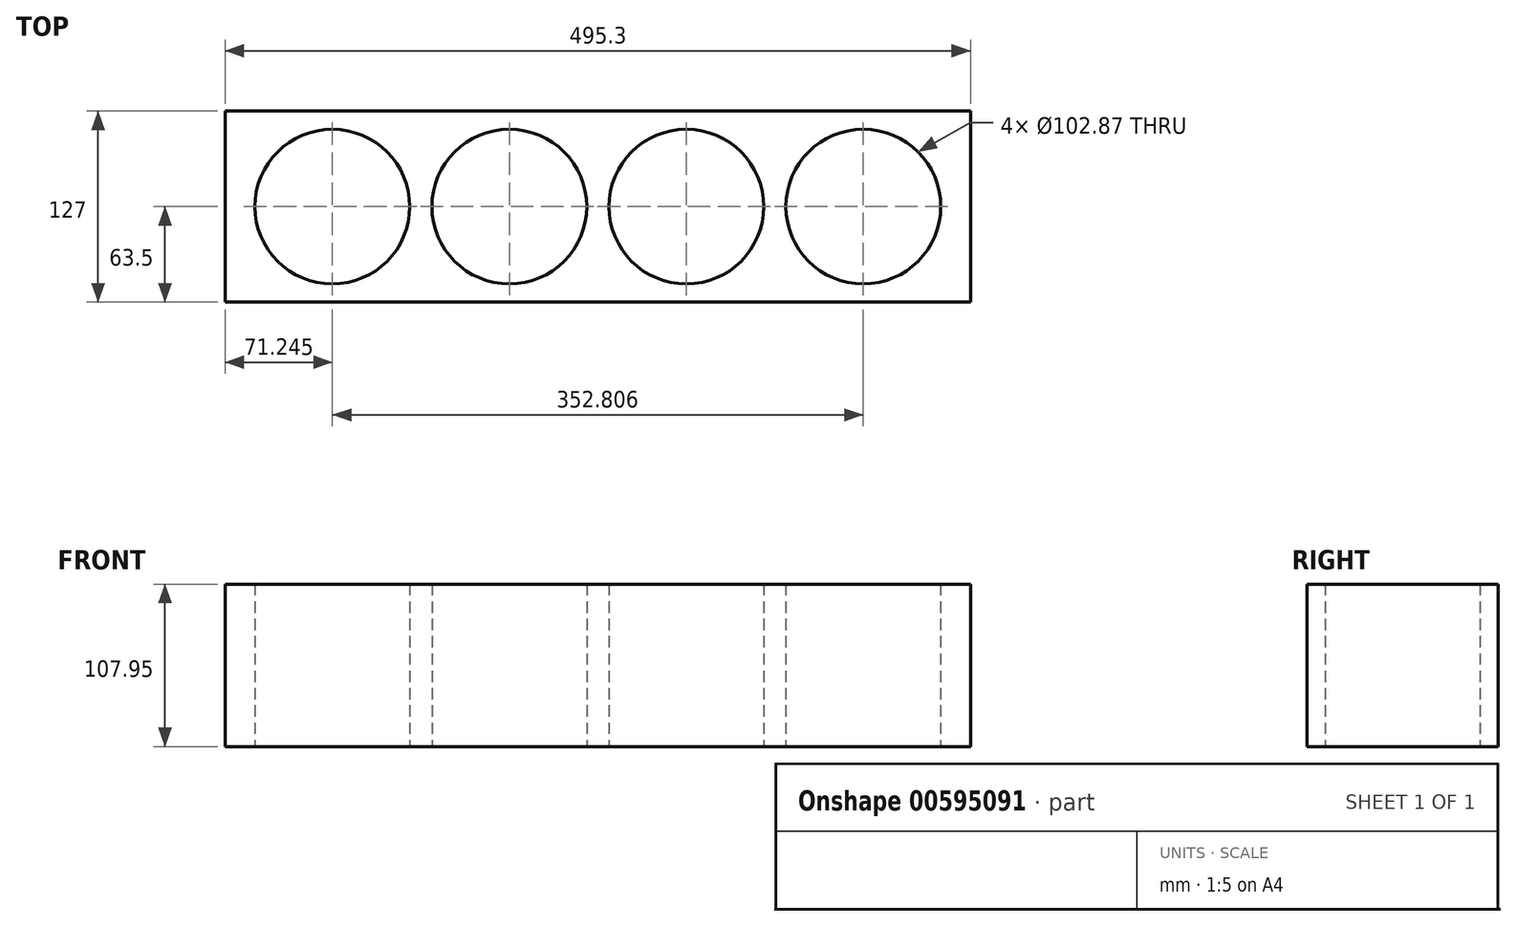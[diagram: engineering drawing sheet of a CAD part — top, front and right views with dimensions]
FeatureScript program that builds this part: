
annotation { "Feature Type Name" : "Feature", "Feature Type Description" : "" }
export const myFeature = defineFeature(function(context is Context, id is Id, definition is map)
    precondition{}
    {
        {
            var Q0;
            Q0=qCreatedBy(makeId("Top.planeOp"),FACE);
            var sketch = newSketch(context, id + "F0", { "sketchPlane" : qUnion([Q0])});
            skCircle(sketch, "E0", {"center": v(-223.26, 0) * mm, "radius": 51.44 * mm});
            skCircle(sketch, "E1.1.0.0", {"center": v(-105.66, 0) * mm, "radius": 51.44 * mm});
            skCircle(sketch, "E1.2.0.0", {"center": v(11.94, 0) * mm, "radius": 51.44 * mm});
            skCircle(sketch, "E1.3.0.0", {"center": v(129.54, 0) * mm, "radius": 51.44 * mm});
            skLineSegment(sketch, "E1.direction1", {"start": v(-223.26, 0) * mm, "end": v(-105.66, 0) * mm, "construction": true});
            skLineSegment(sketch, "E2", {"start": v(-223.26, 0) * mm, "end": v(129.54, 0) * mm, "construction": true});
            skLineSegment(sketch, "E3.bottom", {"start": v(200.79, 63.5) * mm, "end": v(-294.51, 63.5) * mm});
            skLineSegment(sketch, "E3.top", {"start": v(200.79, -63.5) * mm, "end": v(-294.51, -63.5) * mm});
            skLineSegment(sketch, "E3.left", {"start": v(200.79, 63.5) * mm, "end": v(200.79, -63.5) * mm});
            skLineSegment(sketch, "E3.right", {"start": v(-294.51, 63.5) * mm, "end": v(-294.51, -63.5) * mm});
            skPoint(sketch, "E3.middle", {"position": v(-46.86, 0) * mm});
            skSolve(sketch);
        }
        {
            var Q0;
            Q0=makeQuery(id+"F0.imprint","IMPRINT",FACE,{"disambiguationData":[TD([[makeQuery(id+"F0.imprint","IMPRINT",EDGE,{"derivedFrom":sQuery(id+"F0.wireOp",EDGE,"E0")}),-1.0]])]});
            extrude(context, id + "F1", {"entities" : qUnion([Q0]), "depth" : 107.95 * mm, "offsetDistance" : 25.4 * mm});
        }
    });
